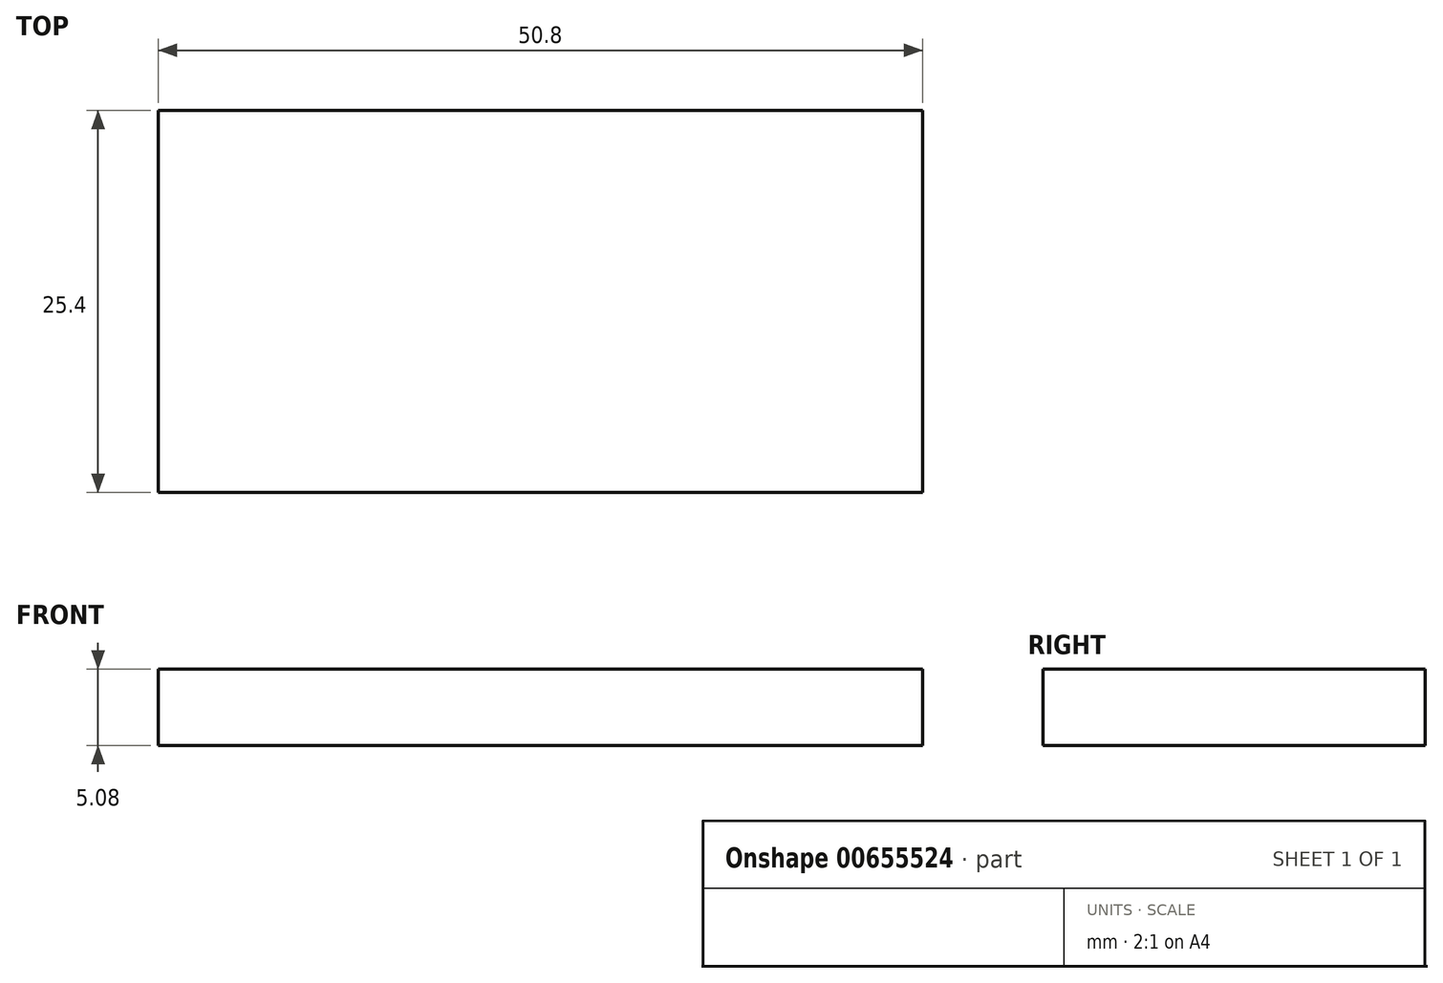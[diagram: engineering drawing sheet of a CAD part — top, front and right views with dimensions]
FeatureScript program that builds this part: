
annotation { "Feature Type Name" : "Feature", "Feature Type Description" : "" }
export const myFeature = defineFeature(function(context is Context, id is Id, definition is map)
    precondition{}
    {
        {
            var Q0;
            Q0=qCreatedBy(makeId("Top.planeOp"),FACE);
            var sketch = newSketch(context, id + "F0", { "sketchPlane" : qUnion([Q0])});
            skLineSegment(sketch, "E0.bottom", {"start": v(25.4, -12.7) * mm, "end": v(-25.4, -12.7) * mm});
            skLineSegment(sketch, "E0.top", {"start": v(25.4, 12.7) * mm, "end": v(-25.4, 12.7) * mm});
            skLineSegment(sketch, "E0.left", {"start": v(25.4, -12.7) * mm, "end": v(25.4, 12.7) * mm});
            skLineSegment(sketch, "E0.right", {"start": v(-25.4, -12.7) * mm, "end": v(-25.4, 12.7) * mm});
            skPoint(sketch, "E0.middle", {"position": v(0, 0) * mm});
            skSolve(sketch);
        }
        {
            var Q0;
            Q0=makeQuery(id+"F0.imprint","IMPRINT",FACE,{"disambiguationData":[TD([[makeQuery(id+"F0.imprint","IMPRINT",EDGE,{"derivedFrom":sQuery(id+"F0.wireOp",EDGE,"E0.bottom")}),-1.0]])]});
            extrude(context, id + "F1", {"entities" : qUnion([Q0]), "depth" : 5.08 * mm, "offsetDistance" : 25.4 * mm});
        }
    });
